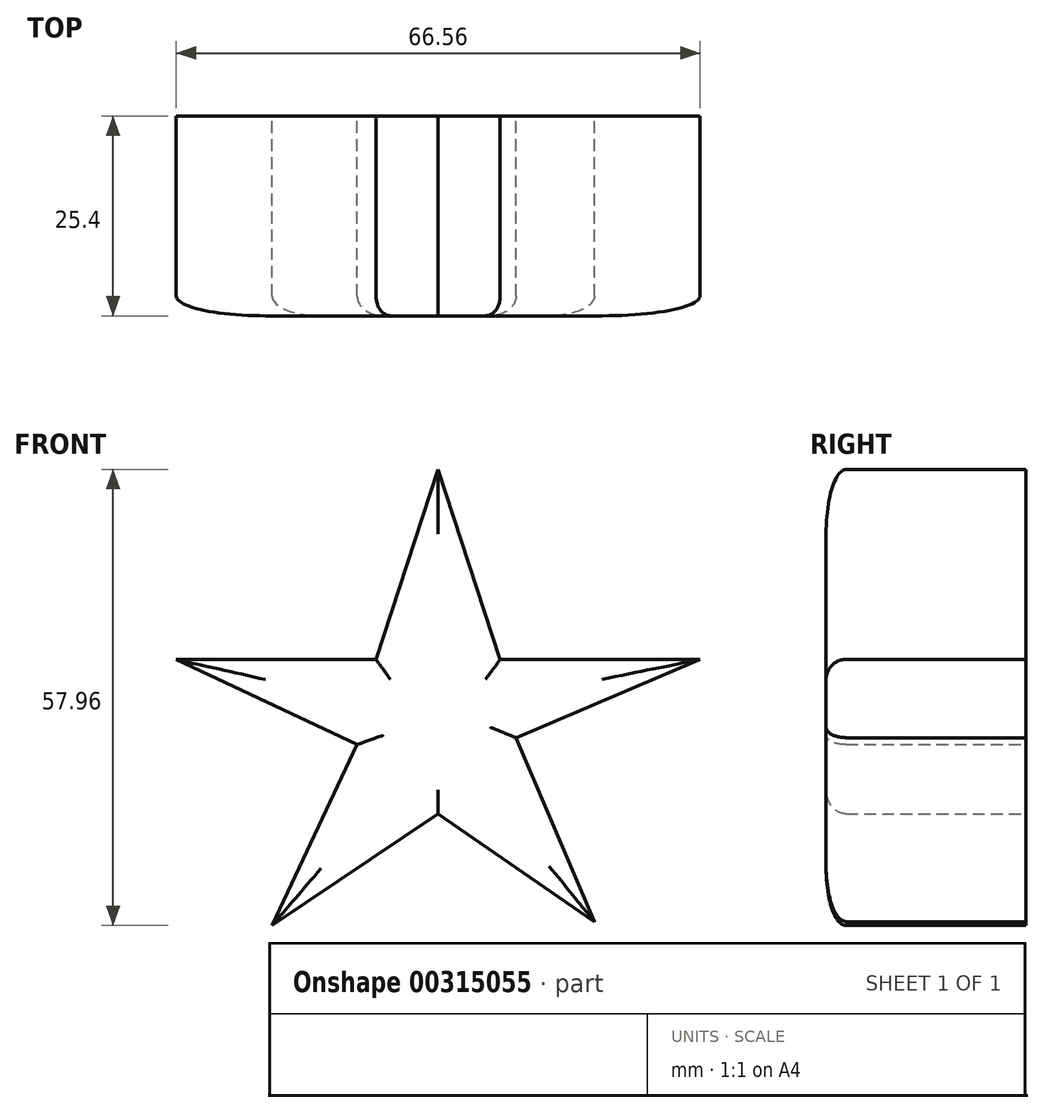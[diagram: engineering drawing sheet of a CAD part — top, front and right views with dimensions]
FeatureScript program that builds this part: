
annotation { "Feature Type Name" : "Feature", "Feature Type Description" : "" }
export const myFeature = defineFeature(function(context is Context, id is Id, definition is map)
    precondition{}
    {
        {
            var Q0;
            Q0=qCreatedBy(makeId("Front.planeOp"),FACE);
            var sketch = newSketch(context, id + "F0", { "sketchPlane" : qUnion([Q0])});
            skLineSegment(sketch, "E0", {"start": v(0, 33.05) * mm, "end": v(-7.84, 8.89) * mm});
            skLineSegment(sketch, "E1", {"start": v(-7.84, 8.89) * mm, "end": v(-33.24, 8.89) * mm});
            skLineSegment(sketch, "E2", {"start": v(-33.24, 8.89) * mm, "end": v(-10.26, -1.92) * mm});
            skLineSegment(sketch, "E3", {"start": v(-10.26, -1.92) * mm, "end": v(-21.06, -24.9) * mm});
            skLineSegment(sketch, "E4", {"start": v(-21.06, -24.9) * mm, "end": v(0, -10.71) * mm});
            skLineSegment(sketch, "E5", {"start": v(0, -10.71) * mm, "end": v(19.9, -24.4) * mm});
            skLineSegment(sketch, "E6", {"start": v(19.9, -24.4) * mm, "end": v(9.95, -1.04) * mm});
            skPoint(sketch, "E6.endSnap0", {"position": v(9.95, -17.56) * mm});
            skLineSegment(sketch, "E7", {"start": v(9.95, -1.04) * mm, "end": v(33.32, 8.91) * mm});
            skLineSegment(sketch, "E8", {"start": v(33.32, 8.91) * mm, "end": v(7.92, 8.91) * mm});
            skLineSegment(sketch, "E9", {"start": v(7.92, 8.91) * mm, "end": v(0, 33.05) * mm});
            skSolve(sketch);
        }
        {
            var Q0;
            Q0 = qSketchRegion(id + "F0", true);
            extrude(context, id + "F1", {"entities" : qUnion([Q0]), "depth" : 25.4 * mm});
        }
        {
            var Q0;
            Q0=makeQuery(id+"F1.opExtrude","CAP_EDGE",EDGE,{"disambiguationData":[OSD([sQuery(id+"F0.wireOp",EDGE,"E1")])],"isStart":false});
            var Q1;
            Q1=makeQuery(id+"F1.opExtrude","CAP_EDGE",EDGE,{"disambiguationData":[OSD([sQuery(id+"F0.wireOp",EDGE,"E2")])],"isStart":false});
            var Q2;
            Q2=makeQuery(id+"F1.opExtrude","CAP_EDGE",EDGE,{"disambiguationData":[OSD([sQuery(id+"F0.wireOp",EDGE,"E3")])],"isStart":false});
            var Q3;
            Q3=makeQuery(id+"F1.opExtrude","CAP_EDGE",EDGE,{"disambiguationData":[OSD([sQuery(id+"F0.wireOp",EDGE,"E4")])],"isStart":false});
            var Q4;
            Q4=makeQuery(id+"F1.opExtrude","CAP_EDGE",EDGE,{"disambiguationData":[OSD([sQuery(id+"F0.wireOp",EDGE,"E5")])],"isStart":false});
            var Q5;
            Q5=makeQuery(id+"F1.opExtrude","CAP_EDGE",EDGE,{"disambiguationData":[OSD([sQuery(id+"F0.wireOp",EDGE,"E6")])],"isStart":false});
            var Q6;
            Q6=makeQuery(id+"F1.opExtrude","CAP_EDGE",EDGE,{"disambiguationData":[OSD([sQuery(id+"F0.wireOp",EDGE,"E7")])],"isStart":false});
            var Q7;
            Q7=makeQuery(id+"F1.opExtrude","CAP_EDGE",EDGE,{"disambiguationData":[OSD([sQuery(id+"F0.wireOp",EDGE,"E8")])],"isStart":false});
            var Q8;
            Q8=makeQuery(id+"F1.opExtrude","CAP_EDGE",EDGE,{"disambiguationData":[OSD([sQuery(id+"F0.wireOp",EDGE,"E9")])],"isStart":false});
            var Q9;
            Q9=makeQuery(id+"F1.opExtrude","CAP_EDGE",EDGE,{"disambiguationData":[OSD([sQuery(id+"F0.wireOp",EDGE,"E0")])],"isStart":false});
            fillet(context, id + "F2", {"entities" : qUnion([Q0, Q1, Q2, Q3, Q4, Q5, Q6, Q7, Q8, Q9]), "radius" : 2.54 * mm, "tangentPropagation" : true, "allowEdgeOverflow" : false});
        }
    });
